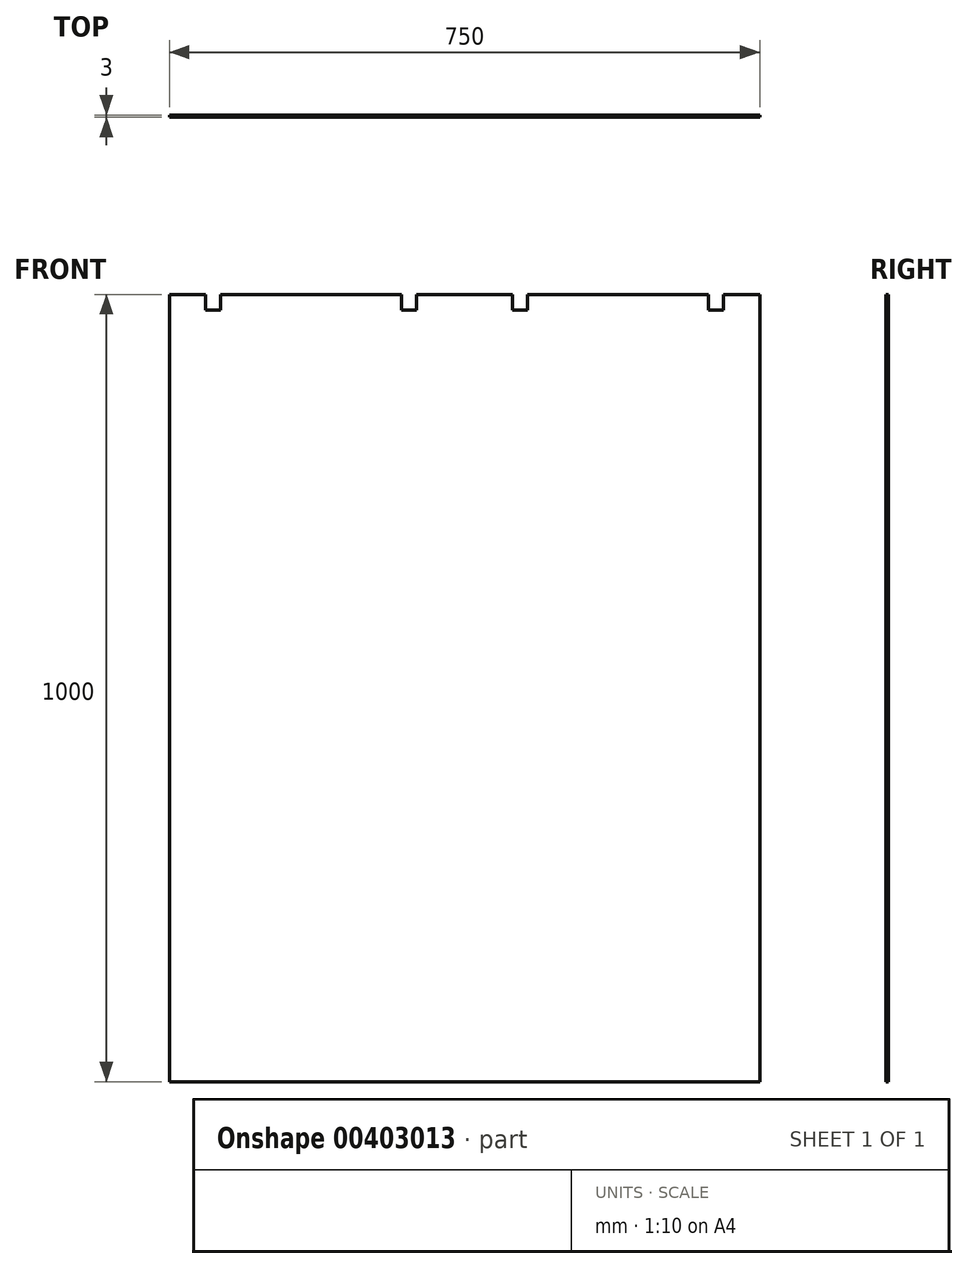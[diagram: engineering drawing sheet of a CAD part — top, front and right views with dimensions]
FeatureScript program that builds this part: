
annotation { "Feature Type Name" : "Feature", "Feature Type Description" : "" }
export const myFeature = defineFeature(function(context is Context, id is Id, definition is map)
    precondition{}
    {
        {
            var Q0;
            Q0=qCreatedBy(makeId("Front.planeOp"),FACE);
            var sketch = newSketch(context, id + "F0", { "sketchPlane" : qUnion([Q0])});
            skLineSegment(sketch, "E0.bottom", {"start": v(0, 0) * mm, "end": v(750, 0) * mm});
            skLineSegment(sketch, "E0.top", {"start": v(0, 1000) * mm, "end": v(46, 1000) * mm});
            skLineSegment(sketch, "E0.left", {"start": v(0, 0) * mm, "end": v(0, 1000) * mm});
            skLineSegment(sketch, "E0.right", {"start": v(750, 0) * mm, "end": v(750, 1000) * mm});
            skLineSegment(sketch, "E1.top", {"start": v(46, 980) * mm, "end": v(65, 980) * mm});
            skLineSegment(sketch, "E1.left", {"start": v(46, 1000) * mm, "end": v(46, 980) * mm});
            skLineSegment(sketch, "E1.right", {"start": v(65, 1000) * mm, "end": v(65, 980) * mm});
            skLineSegment(sketch, "E2.top", {"start": v(685, 980) * mm, "end": v(704, 980) * mm});
            skLineSegment(sketch, "E2.left", {"start": v(685, 1000) * mm, "end": v(685, 980) * mm});
            skLineSegment(sketch, "E2.right", {"start": v(704, 1000) * mm, "end": v(704, 980) * mm});
            skLineSegment(sketch, "E3.trimOffspring", {"start": v(65, 1000) * mm, "end": v(295, 1000) * mm});
            skLineSegment(sketch, "E4.trimOffspring", {"start": v(704, 1000) * mm, "end": v(750, 1000) * mm});
            skLineSegment(sketch, "E5.top", {"start": v(295, 980) * mm, "end": v(314, 980) * mm});
            skLineSegment(sketch, "E5.left", {"start": v(295, 1000) * mm, "end": v(295, 980) * mm});
            skLineSegment(sketch, "E5.right", {"start": v(314, 1000) * mm, "end": v(314, 980) * mm});
            skLineSegment(sketch, "E6.trimOffspring", {"start": v(314, 1000) * mm, "end": v(436, 1000) * mm});
            skLineSegment(sketch, "E7.top", {"start": v(436, 980) * mm, "end": v(455, 980) * mm});
            skLineSegment(sketch, "E7.left", {"start": v(436, 1000) * mm, "end": v(436, 980) * mm});
            skLineSegment(sketch, "E7.right", {"start": v(455, 1000) * mm, "end": v(455, 980) * mm});
            skLineSegment(sketch, "E8.trimOffspring", {"start": v(455, 1000) * mm, "end": v(685, 1000) * mm});
            skSolve(sketch);
        }
        {
            var Q0;
            Q0=makeQuery(id+"F0.imprint","IMPRINT",FACE,{"disambiguationData":[TD([[makeQuery(id+"F0.imprint","IMPRINT",EDGE,{"derivedFrom":sQuery(id+"F0.wireOp",EDGE,"E0.bottom")}),1.0]])]});
            extrude(context, id + "F1", {"entities" : qUnion([Q0]), "depth" : 3 * mm});
        }
    });
